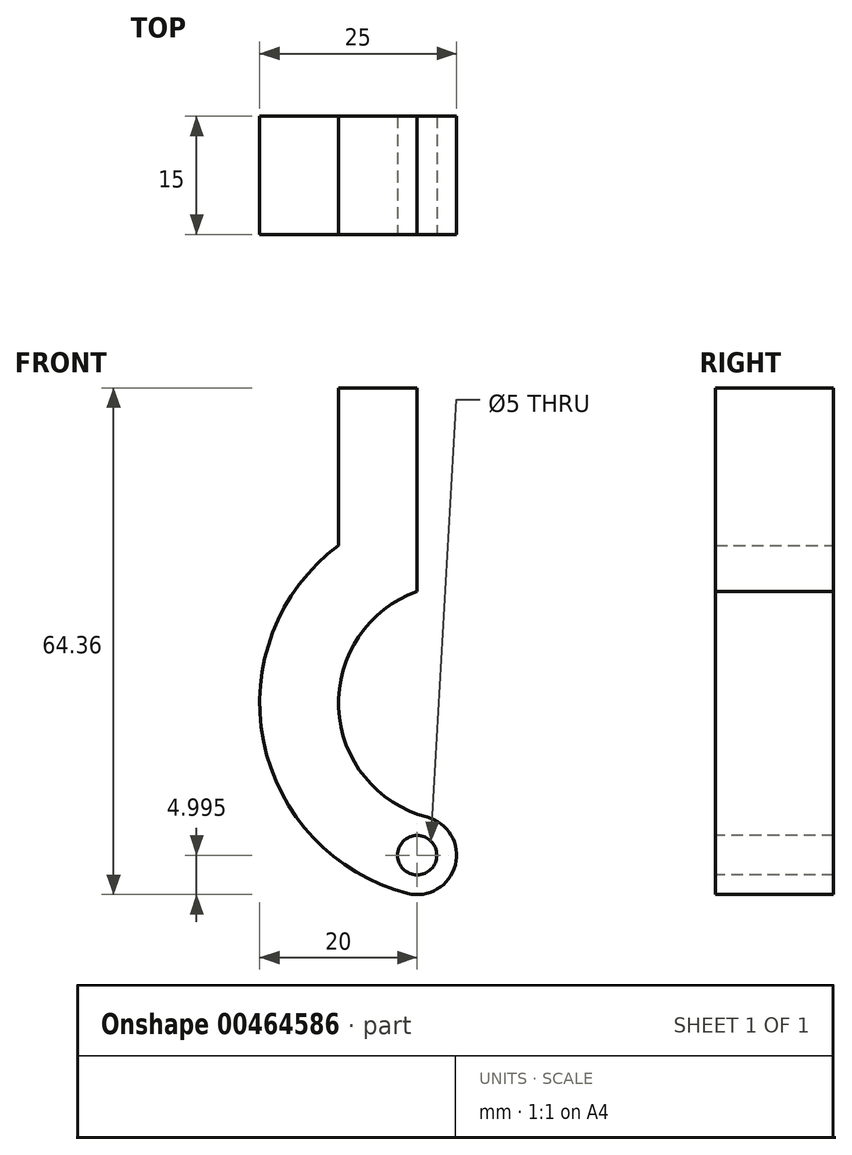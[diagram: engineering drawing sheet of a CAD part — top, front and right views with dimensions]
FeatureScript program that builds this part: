
annotation { "Feature Type Name" : "Feature", "Feature Type Description" : "" }
export const myFeature = defineFeature(function(context is Context, id is Id, definition is map)
    precondition{}
    {
        {
            var Q0;
            Q0=qCreatedBy(makeId("Front.planeOp"),FACE);
            var sketch = newSketch(context, id + "F0", { "sketchPlane" : qUnion([Q0])});
            skArc(sketch, "E0", {"start": v(-15, 20) * mm, "mid": v(-23.72, -7.9) * mm, "end": v(0, -25) * mm});
            skArc(sketch, "E1", {"start": v(-5, 14.14) * mm, "mid": v(-14.78, -2.54) * mm, "end": v(0, -15) * mm});
            skLineSegment(sketch, "E2", {"start": v(0, 0) * mm, "end": v(0, 15) * mm, "construction": true});
            skLineSegment(sketch, "E3", {"start": v(0, 40) * mm, "end": v(5, 40) * mm, "construction": true});
            skLineSegment(sketch, "E4", {"start": v(0, 40) * mm, "end": v(-5, 40) * mm, "construction": true});
            skLineSegment(sketch, "E5", {"start": v(-5, 40) * mm, "end": v(-15, 40) * mm});
            skLineSegment(sketch, "E6", {"start": v(-15, 40) * mm, "end": v(-15, 20) * mm});
            skLineSegment(sketch, "E7", {"start": v(-5, 14.14) * mm, "end": v(-5, 40) * mm});
            skLineSegment(sketch, "E8", {"start": v(0, 0) * mm, "end": v(0, -14.15) * mm, "construction": true});
            skLineSegment(sketch, "E9", {"start": v(0, -14.15) * mm, "end": v(10.43, -14.15) * mm, "construction": true});
            skLineSegment(sketch, "E10", {"start": v(0, -14.15) * mm, "end": v(-10.43, -14.15) * mm, "construction": true});
            skLineSegment(sketch, "E11", {"start": v(0, -15) * mm, "end": v(0, -25) * mm});
            skLineSegment(sketch, "E12", {"start": v(0, 25) * mm, "end": v(0, 15) * mm});
            skLineSegment(sketch, "E13.trimOffspring", {"start": v(0, 25) * mm, "end": v(0, 40) * mm, "construction": true});
            skPoint(sketch, "E14.orphan", {"position": v(-5, 12) * mm});
            skSolve(sketch);
        }
        {
            var Q0;
            Q0 = qSketchRegion(id + "F0", true);
            extrude(context, id + "F1", {"entities" : qUnion([Q0]), "depth" : 15 * mm});
        }
        {
            var Q0;
            Q0=makeQuery(id+"F1.opExtrude","SWEPT_EDGE",EDGE,{"disambiguationData":[OSD([sQuery(id+"F0.wireOp",EDGE,"E0"),sQuery(id+"F0.wireOp",EDGE,"E11")])]});
            var Q1;
            Q1=makeQuery(id+"F1.opExtrude","SWEPT_EDGE",EDGE,{"disambiguationData":[OSD([sQuery(id+"F0.wireOp",EDGE,"E1"),sQuery(id+"F0.wireOp",EDGE,"E11")])]});
            fillet(context, id + "F2", {"entities" : qUnion([Q0, Q1]), "radius" : 5 * mm, "tangentPropagation" : true, "allowEdgeOverflow" : false});
        }
        {
            var Q0;
            Q0=makeQuery(id+"F1.opExtrude","CAP_FACE",FACE,{"disambiguationData":[OSD([sQuery(id+"F0.wireOp",EDGE,"E0"),sQuery(id+"F0.wireOp",EDGE,"E1"),sQuery(id+"F0.wireOp",EDGE,"E5"),sQuery(id+"F0.wireOp",EDGE,"E6"),sQuery(id+"F0.wireOp",EDGE,"E7"),sQuery(id+"F0.wireOp",EDGE,"E11")])],"isStart":false});
            var sketch = newSketch(context, id + "F3", { "sketchPlane" : qUnion([Q0])});
            skCircle(sketch, "E15", {"center": v(-5, -19.36) * mm, "radius": 2.5 * mm});
            skSolve(sketch);
        }
        {
            var Q0;
            Q0 = qSketchRegion(id + "F3", true);
            extrude(context, id + "F4", {"entities" : qUnion([Q0]), "operationType" : NewBodyOperationType.REMOVE, "endBound" : BoundingType.THROUGH_ALL, "oppositeDirection" : true, "depth" : 25 * mm});
        }
    });
